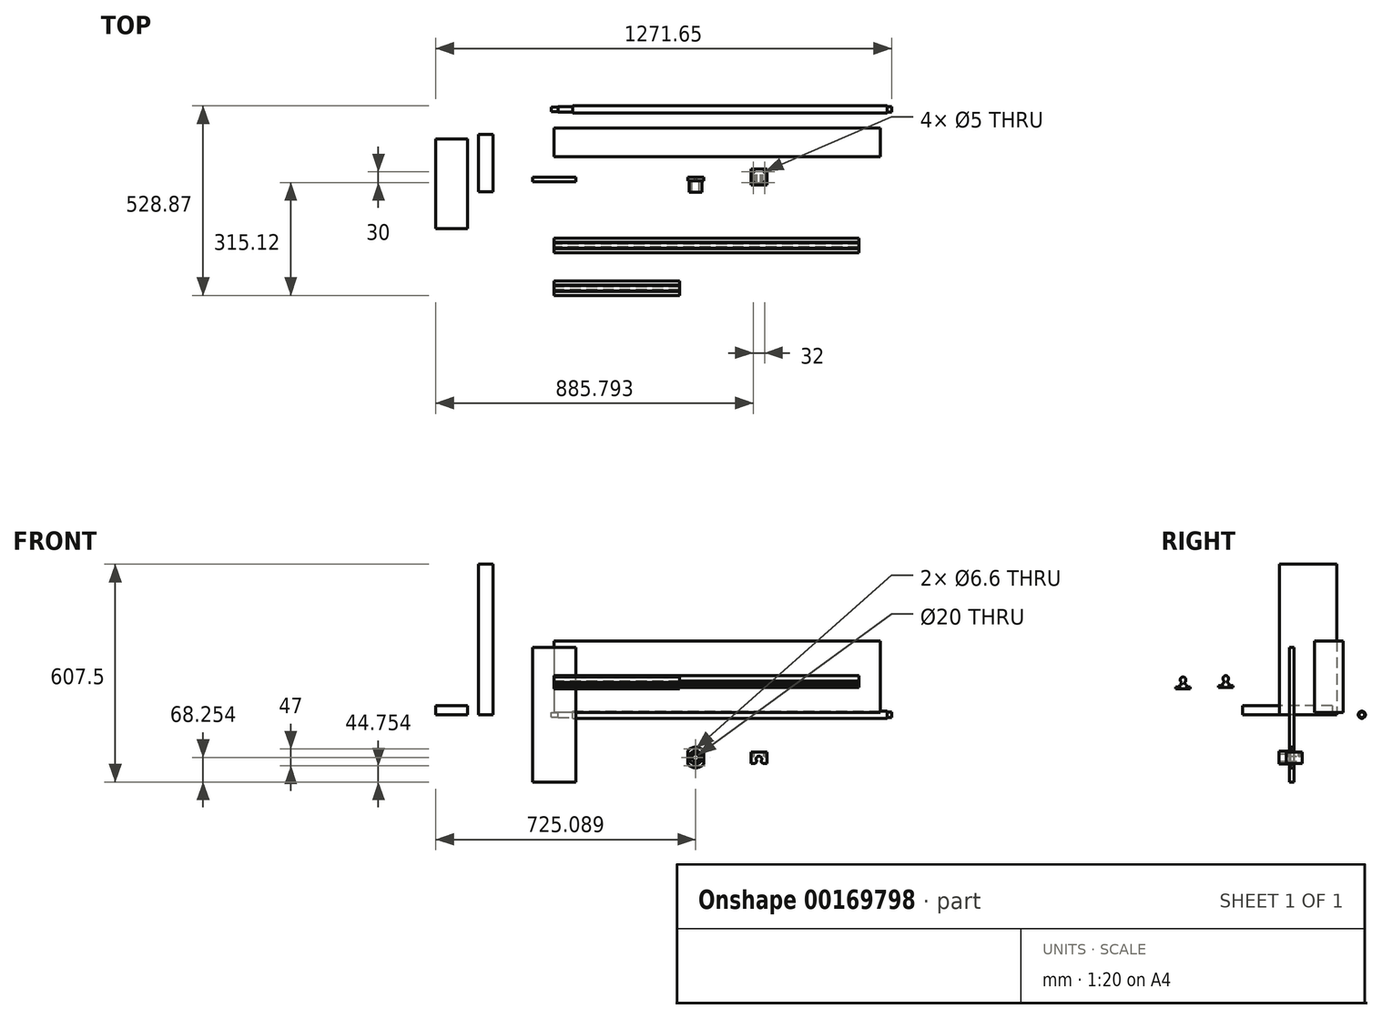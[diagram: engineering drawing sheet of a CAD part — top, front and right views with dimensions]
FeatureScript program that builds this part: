
annotation { "Feature Type Name" : "Feature", "Feature Type Description" : "" }
export const myFeature = defineFeature(function(context is Context, id is Id, definition is map)
    precondition{}
    {
        {
            var Q0;
            Q0=qCreatedBy(makeId("Front.planeOp"),FACE);
            var sketch = newSketch(context, id + "F0", { "sketchPlane" : qUnion([Q0])});
            skLineSegment(sketch, "E0.bottom", {"start": v(-60, -187.5) * mm, "end": v(60, -187.5) * mm});
            skLineSegment(sketch, "E0.top", {"start": v(-60, 187.5) * mm, "end": v(60, 187.5) * mm});
            skLineSegment(sketch, "E0.left", {"start": v(-60, -187.5) * mm, "end": v(-60, 187.5) * mm});
            skLineSegment(sketch, "E0.right", {"start": v(60, -187.5) * mm, "end": v(60, 187.5) * mm});
            skPoint(sketch, "E0.middle", {"position": v(0, 0) * mm});
            skSolve(sketch);
        }
        {
            var Q0;
            Q0=qSketchRegion(id+"F0",true);
            extrude(context, id + "F1", {"entities" : qUnion([Q0]), "depth" : 12.7 * mm});
        }
        {
            var Q0;
            Q0=qCreatedBy(makeId("Right.planeOp"),FACE);
            var sketch = newSketch(context, id + "F2", { "sketchPlane" : qUnion([Q0])});
            skLineSegment(sketch, "E1.bottom", {"start": v(56.93, 206.24) * mm, "end": v(136.93, 206.24) * mm});
            skLineSegment(sketch, "E1.top", {"start": v(56.93, 6.24) * mm, "end": v(136.93, 6.24) * mm});
            skLineSegment(sketch, "E1.left", {"start": v(56.93, 206.24) * mm, "end": v(56.93, 6.24) * mm});
            skLineSegment(sketch, "E1.right", {"start": v(136.93, 206.24) * mm, "end": v(136.93, 6.24) * mm});
            skSolve(sketch);
        }
        {
            var Q0;
            Q0 = qSketchRegion(id + "F2", true);
            extrude(context, id + "F3", {"entities" : qUnion([Q0]), "depth" : 910 * mm, "offsetDistance" : 25 * mm});
        }
        {
            var Q0;
            Q0=qCreatedBy(makeId("Top.planeOp"),FACE);
            var sketch = newSketch(context, id + "F4", { "sketchPlane" : qUnion([Q0])});
            skLineSegment(sketch, "E2.bottom", {"start": v(-211.04, 118.79) * mm, "end": v(-171.04, 118.79) * mm});
            skLineSegment(sketch, "E2.top", {"start": v(-211.04, -41.21) * mm, "end": v(-171.04, -41.21) * mm});
            skLineSegment(sketch, "E2.left", {"start": v(-211.04, 118.79) * mm, "end": v(-211.04, -41.21) * mm});
            skLineSegment(sketch, "E2.right", {"start": v(-171.04, 118.79) * mm, "end": v(-171.04, -41.21) * mm});
            skSolve(sketch);
        }
        {
            var Q0;
            Q0 = qSketchRegion(id + "F4", true);
            extrude(context, id + "F5", {"entities" : qUnion([Q0]), "depth" : 420 * mm});
        }
        {
            var Q0;
            Q0=qCreatedBy(makeId("Top.planeOp"),FACE);
            var sketch = newSketch(context, id + "F6", { "sketchPlane" : qUnion([Q0])});
            skLineSegment(sketch, "E3.bottom", {"start": v(-330.42, 106.27) * mm, "end": v(-241.52, 106.27) * mm});
            skLineSegment(sketch, "E3.top", {"start": v(-330.42, -143.73) * mm, "end": v(-241.52, -143.73) * mm});
            skLineSegment(sketch, "E3.left", {"start": v(-330.42, 106.27) * mm, "end": v(-330.42, -143.73) * mm});
            skLineSegment(sketch, "E3.right", {"start": v(-241.52, 106.27) * mm, "end": v(-241.52, -143.73) * mm});
            skSolve(sketch);
        }
        {
            var Q0;
            Q0 = qSketchRegion(id + "F6", true);
            extrude(context, id + "F7", {"entities" : qUnion([Q0]), "depth" : 25.4 * mm});
        }
        {
            var Q0;
            Q0=qCreatedBy(makeId("Front.planeOp"),FACE);
            var sketch = newSketch(context, id + "F8", { "sketchPlane" : qUnion([Q0])});
            skLineSegment(sketch, "E4.bottom", {"start": v(593.87, -103.59) * mm, "end": v(548.87, -103.59) * mm});
            skLineSegment(sketch, "E4.top", {"start": v(593.87, -136.59) * mm, "end": v(582.28, -136.59) * mm});
            skLineSegment(sketch, "E4.left", {"start": v(593.87, -103.59) * mm, "end": v(593.87, -136.59) * mm});
            skLineSegment(sketch, "E4.right", {"start": v(548.87, -103.59) * mm, "end": v(548.87, -136.59) * mm});
            skArc(sketch, "E5", {"start": v(576.52, -129.71) * mm, "mid": v(571.37, -115.59) * mm, "end": v(566.23, -129.71) * mm});
            skPoint(sketch, "E5.centerSnap0", {"position": v(571.37, -103.59) * mm});
            skLineSegment(sketch, "E6", {"start": v(571.37, -103.59) * mm, "end": v(571.37, -123.59) * mm, "construction": true});
            skLineSegment(sketch, "E7", {"start": v(576.52, -129.71) * mm, "end": v(582.28, -136.59) * mm});
            skLineSegment(sketch, "E8", {"start": v(566.23, -129.71) * mm, "end": v(560.46, -136.59) * mm});
            skLineSegment(sketch, "E9.trimOffspring", {"start": v(560.46, -136.59) * mm, "end": v(548.87, -136.59) * mm});
            skSolve(sketch);
        }
        {
            var Q0;
            Q0=makeQuery(id+"F8.imprint","IMPRINT",FACE,{"disambiguationData":[TD([[makeQuery(id+"F8.imprint","IMPRINT",EDGE,{"derivedFrom":sQuery(id+"F8.wireOp",EDGE,"E4.bottom")}),1.0]])]});
            extrude(context, id + "F9", {"entities" : qUnion([Q0]), "endBound" : BoundingType.SYMMETRIC, "depth" : 45 * mm, "offsetDistance" : 25 * mm});
        }
        {
            var Q0;
            Q0=makeQuery(id+"F9.opExtrude","SWEPT_FACE",FACE,{"disambiguationData":[OSD([sQuery(id+"F8.wireOp",EDGE,"E4.bottom")])]});
            var sketch = newSketch(context, id + "F10", { "sketchPlane" : qUnion([Q0])});
            skLineSegment(sketch, "E10.bottom", {"start": v(555.37, 15) * mm, "end": v(587.37, 15) * mm, "construction": true});
            skLineSegment(sketch, "E10.top", {"start": v(555.37, -15) * mm, "end": v(587.37, -15) * mm, "construction": true});
            skLineSegment(sketch, "E10.left", {"start": v(555.37, 15) * mm, "end": v(555.37, -15) * mm, "construction": true});
            skLineSegment(sketch, "E10.right", {"start": v(587.37, 15) * mm, "end": v(587.37, -15) * mm, "construction": true});
            skLineSegment(sketch, "E11", {"start": v(555.37, 0) * mm, "end": v(548.87, 0) * mm, "construction": true});
            skLineSegment(sketch, "E12", {"start": v(571.37, 15) * mm, "end": v(571.37, 22.5) * mm, "construction": true});
            skSolve(sketch);
        }
        {
            var Q0;
            Q0=sQuery(id+"F10.wireOp",VERTEX,"E10.bottom.start");
            var Q1;
            Q1=sQuery(id+"F10.wireOp",VERTEX,"E10.bottom.end");
            var Q2;
            Q2=sQuery(id+"F10.wireOp",VERTEX,"E10.top.end");
            var Q3;
            Q3=sQuery(id+"F10.wireOp",VERTEX,"E10.top.start");
            var Q4;
            Q4=makeQuery(id+"F9.opExtrude","SWEPT_BODY",BODY,{"disambiguationData":[OSD([sQuery(id+"F8.wireOp",EDGE,"E4.bottom"),sQuery(id+"F8.wireOp",EDGE,"E4.top"),sQuery(id+"F8.wireOp",EDGE,"E4.left"),sQuery(id+"F8.wireOp",EDGE,"E4.right"),sQuery(id+"F8.wireOp",EDGE,"E5"),sQuery(id+"F8.wireOp",EDGE,"E7"),sQuery(id+"F8.wireOp",EDGE,"E8"),sQuery(id+"F8.wireOp",EDGE,"E9.trimOffspring")])]});
            hole(context, id + "F11", {"style" : HoleStyle.SIMPLE, "endStyle" : HoleEndStyle.BLIND, "holeDiameter" : 5 * mm, "holeDepth" : 12 * mm, "isTappedThrough" : true, "tappedDepth" : 12 * mm, "tapClearance" : 3, "locations" : qUnion([Q0, Q1, Q2, Q3]), "scope" : qUnion([Q4])});
        }
        {
            var Q0;
            Q0=qCreatedBy(makeId("Front.planeOp"),FACE);
            var sketch = newSketch(context, id + "F12", { "sketchPlane" : qUnion([Q0])});
            skArc(sketch, "E13", {"start": v(416.67, -100.35) * mm, "mid": v(394.67, -90.25) * mm, "end": v(372.67, -100.35) * mm});
            skLineSegment(sketch, "E14", {"start": v(372.67, -100.35) * mm, "end": v(372.67, -138.14) * mm});
            skLineSegment(sketch, "E15", {"start": v(416.67, -138.14) * mm, "end": v(416.67, -100.35) * mm});
            skArc(sketch, "E16.trimOffspring", {"start": v(372.67, -138.14) * mm, "mid": v(394.67, -148.25) * mm, "end": v(416.67, -138.14) * mm});
            skCircle(sketch, "E17", {"center": v(394.67, -119.25) * mm, "radius": 10 * mm});
            skLineSegment(sketch, "E18", {"start": v(394.67, -95.75) * mm, "end": v(394.67, -142.75) * mm, "construction": true});
            skCircle(sketch, "E19", {"center": v(394.67, -95.75) * mm, "radius": 3.3 * mm});
            skCircle(sketch, "E20", {"center": v(394.67, -142.75) * mm, "radius": 3.3 * mm});
            skSolve(sketch);
        }
        {
            var Q0;
            Q0 = qSketchRegion(id + "F12", true);
            extrude(context, id + "F13", {"entities" : qUnion([Q0]), "depth" : 10 * mm, "offsetDistance" : 25 * mm});
        }
        {
            var Q0;
            Q0=makeQuery(id+"F13.opExtrude","CAP_FACE",FACE,{"disambiguationData":[OSD([sQuery(id+"F12.wireOp",EDGE,"E13"),sQuery(id+"F12.wireOp",EDGE,"E14"),sQuery(id+"F12.wireOp",EDGE,"E15"),sQuery(id+"F12.wireOp",EDGE,"E16.trimOffspring"),sQuery(id+"F12.wireOp",EDGE,"E17")])],"isStart":false});
            var sketch = newSketch(context, id + "F14", { "sketchPlane" : qUnion([Q0])});
            skCircle(sketch, "E21", {"center": v(394.67, -119.25) * mm, "radius": 18 * mm});
            skCircle(sketch, "E22.0", {"center": v(394.67, -119.25) * mm, "radius": 10 * mm});
            skSolve(sketch);
        }
        {
            var Q0;
            Q0 = qSketchRegion(id + "F14", true);
            extrude(context, id + "F15", {"entities" : qUnion([Q0]), "operationType" : NewBodyOperationType.ADD, "depth" : 32 * mm, "offsetDistance" : 25 * mm});
        }
        {
            var Q0;
            Q0=qCreatedBy(makeId("Top.planeOp"),FACE);
            var sketch = newSketch(context, id + "F16", { "sketchPlane" : qUnion([Q0])});
            skLineSegment(sketch, "E23", {"start": v(-8.77, 188.75) * mm, "end": v(-72.85, 188.75) * mm, "construction": true});
            skLineSegment(sketch, "E24", {"start": v(-8.77, 188.75) * mm, "end": v(-8.77, 194.75) * mm});
            skLineSegment(sketch, "E25", {"start": v(-8.77, 194.75) * mm, "end": v(11.23, 194.75) * mm});
            skLineSegment(sketch, "E26", {"start": v(11.23, 194.75) * mm, "end": v(11.23, 196.25) * mm});
            skLineSegment(sketch, "E27", {"start": v(11.23, 196.25) * mm, "end": v(51.23, 196.25) * mm});
            skLineSegment(sketch, "E28", {"start": v(51.23, 196.25) * mm, "end": v(51.23, 198.75) * mm});
            skLineSegment(sketch, "E29", {"start": v(51.23, 198.75) * mm, "end": v(929.23, 198.75) * mm});
            skLineSegment(sketch, "E30", {"start": v(929.23, 198.75) * mm, "end": v(929.23, 196.25) * mm});
            skLineSegment(sketch, "E31", {"start": v(929.23, 196.25) * mm, "end": v(941.23, 196.25) * mm});
            skLineSegment(sketch, "E32", {"start": v(941.23, 196.25) * mm, "end": v(941.23, 188.75) * mm});
            skLineSegment(sketch, "E33", {"start": v(941.23, 188.75) * mm, "end": v(-8.77, 188.75) * mm});
            skSolve(sketch);
        }
        {
            var Q0;
            Q0 = qSketchRegion(id + "F16", true);
            var Q1;
            Q1=sQuery(id+"F16.wireOp",EDGE,"E23");
            revolve(context, id + "F17", {"entities" : qUnion([Q0]), "axis" : qUnion([Q1]), "revolveType" : RevolveType.FULL});
        }
        {
            var Q0;
            Q0=qCreatedBy(makeId("Right.planeOp"),FACE);
            var sketch = newSketch(context, id + "F18", { "sketchPlane" : qUnion([Q0])});
            skLineSegment(sketch, "E34.bottom", {"start": v(-210.96, 75.77) * mm, "end": v(-170.96, 75.77) * mm});
            skLineSegment(sketch, "E35", {"start": v(-210.96, 75.77) * mm, "end": v(-210.96, 80.77) * mm});
            skLineSegment(sketch, "E36", {"start": v(-200.2, 87.47) * mm, "end": v(-197.16, 87.47) * mm});
            skLineSegment(sketch, "E37", {"start": v(-197.16, 87.47) * mm, "end": v(-194.34, 93.52) * mm});
            skLineSegment(sketch, "E38", {"start": v(-187.57, 93.52) * mm, "end": v(-184.75, 87.47) * mm});
            skLineSegment(sketch, "E39", {"start": v(-184.75, 87.47) * mm, "end": v(-181.7, 87.47) * mm});
            skLineSegment(sketch, "E40", {"start": v(-170.96, 80.77) * mm, "end": v(-170.96, 75.77) * mm});
            skArc(sketch, "E41", {"start": v(-187.57, 93.52) * mm, "mid": v(-190.96, 108.77) * mm, "end": v(-194.34, 93.52) * mm});
            skLineSegment(sketch, "E42", {"start": v(-190.96, 100.77) * mm, "end": v(-190.96, 75.77) * mm, "construction": true});
            skLineSegment(sketch, "E43", {"start": v(-200.2, 87.47) * mm, "end": v(-200.2, 80.77) * mm});
            skLineSegment(sketch, "E44", {"start": v(-200.2, 80.77) * mm, "end": v(-210.96, 80.77) * mm});
            skLineSegment(sketch, "E45", {"start": v(-181.7, 87.47) * mm, "end": v(-181.7, 80.77) * mm});
            skLineSegment(sketch, "E46", {"start": v(-181.7, 80.77) * mm, "end": v(-170.96, 80.77) * mm});
            skSolve(sketch);
        }
        {
            var Q0;
            Q0=makeQuery(id+"F18.imprint","IMPRINT",FACE,{"disambiguationData":[TD([[makeQuery(id+"F18.imprint","IMPRINT",EDGE,{"derivedFrom":sQuery(id+"F18.wireOp",EDGE,"E34.bottom")}),1.0]])]});
            extrude(context, id + "F19", {"entities" : qUnion([Q0]), "depth" : 850 * mm, "offsetDistance" : 25 * mm});
        }
        {
            var Q0;
            Q0=qCreatedBy(makeId("Right.planeOp"),FACE);
            var sketch = newSketch(context, id + "F20", { "sketchPlane" : qUnion([Q0])});
            skLineSegment(sketch, "E47.bottom", {"start": v(-330.12, 72.28) * mm, "end": v(-290.12, 72.28) * mm});
            skLineSegment(sketch, "E48", {"start": v(-330.12, 72.28) * mm, "end": v(-330.12, 77.28) * mm});
            skLineSegment(sketch, "E49", {"start": v(-319.37, 83.98) * mm, "end": v(-316.32, 83.98) * mm});
            skLineSegment(sketch, "E50", {"start": v(-316.32, 83.98) * mm, "end": v(-313.5, 90.02) * mm});
            skLineSegment(sketch, "E51", {"start": v(-306.74, 90.02) * mm, "end": v(-303.92, 83.98) * mm});
            skLineSegment(sketch, "E52", {"start": v(-303.92, 83.98) * mm, "end": v(-300.87, 83.98) * mm});
            skLineSegment(sketch, "E53", {"start": v(-290.12, 77.28) * mm, "end": v(-290.12, 72.28) * mm});
            skArc(sketch, "E54", {"start": v(-306.74, 90.02) * mm, "mid": v(-310.12, 105.28) * mm, "end": v(-313.5, 90.02) * mm});
            skLineSegment(sketch, "E55", {"start": v(-310.12, 97.28) * mm, "end": v(-310.12, 72.28) * mm, "construction": true});
            skLineSegment(sketch, "E56", {"start": v(-319.37, 83.98) * mm, "end": v(-319.37, 77.28) * mm});
            skLineSegment(sketch, "E57", {"start": v(-319.37, 77.28) * mm, "end": v(-330.12, 77.28) * mm});
            skLineSegment(sketch, "E58", {"start": v(-300.87, 83.98) * mm, "end": v(-300.87, 77.28) * mm});
            skLineSegment(sketch, "E59", {"start": v(-300.87, 77.28) * mm, "end": v(-290.12, 77.28) * mm});
            skSolve(sketch);
        }
        {
            var Q0;
            Q0=makeQuery(id+"F20.imprint","IMPRINT",FACE,{"disambiguationData":[TD([[makeQuery(id+"F20.imprint","IMPRINT",EDGE,{"derivedFrom":sQuery(id+"F20.wireOp",EDGE,"E47.bottom")}),1.0]])]});
            extrude(context, id + "F21", {"entities" : qUnion([Q0]), "depth" : 350 * mm, "offsetDistance" : 25 * mm});
        }
    });
